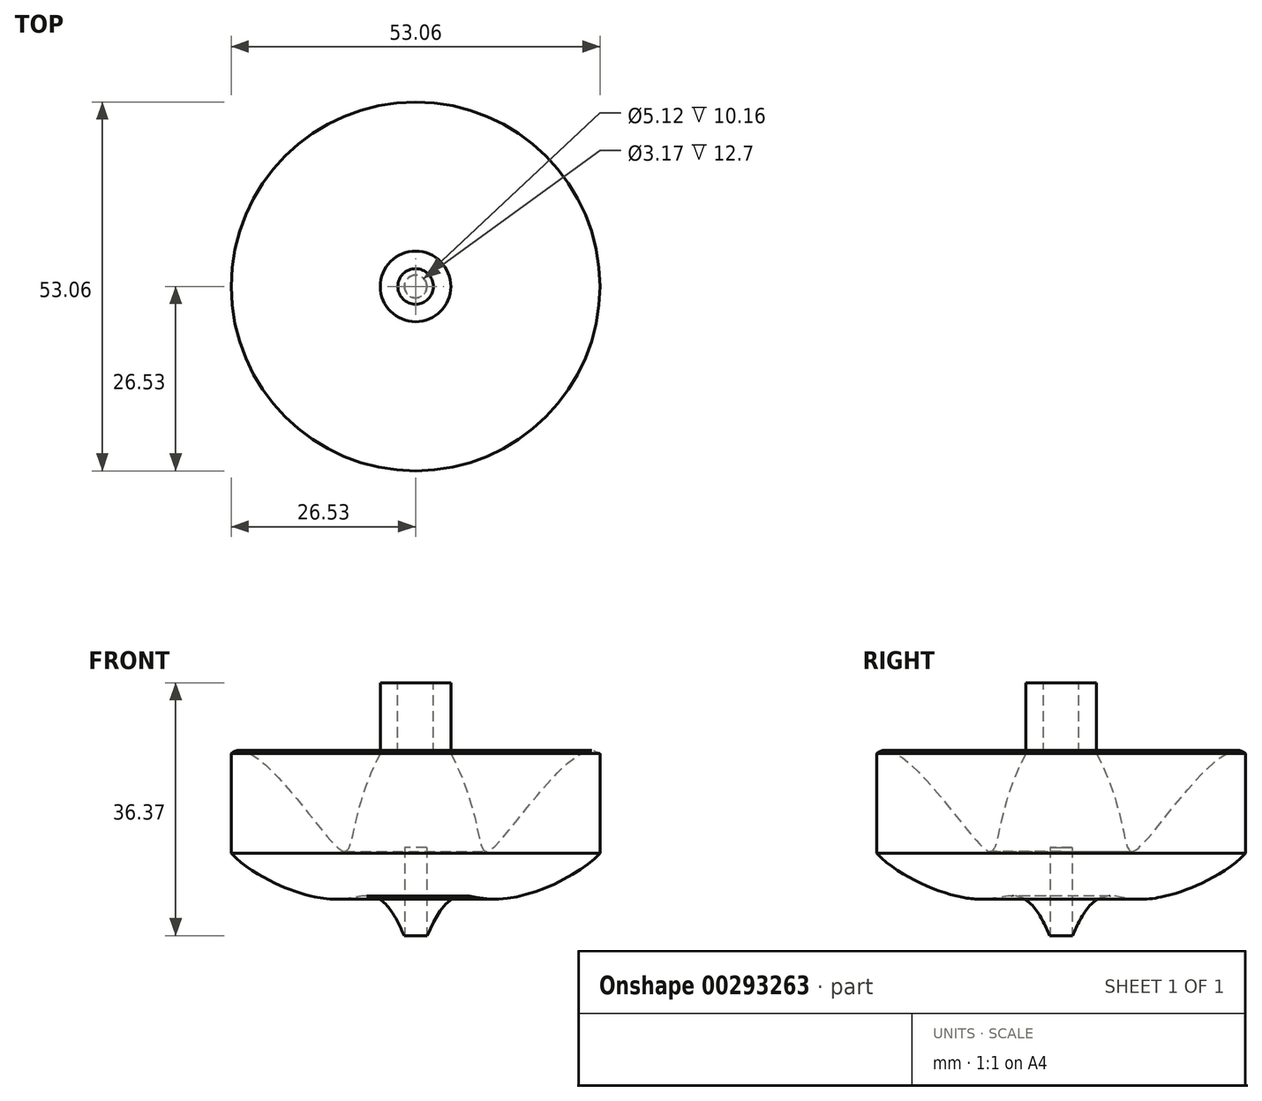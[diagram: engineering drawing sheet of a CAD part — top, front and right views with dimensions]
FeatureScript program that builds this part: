
annotation { "Feature Type Name" : "Feature", "Feature Type Description" : "" }
export const myFeature = defineFeature(function(context is Context, id is Id, definition is map)
    precondition{}
    {
        {
            var Q0;
            Q0=qCreatedBy(makeId("Front.planeOp"),FACE);
            var sketch = newSketch(context, id + "F0", { "sketchPlane" : qUnion([Q0])});
            skLineSegment(sketch, "E0", {"start": v(0, 0) * mm, "end": v(1.65, 0) * mm});
            skPoint(sketch, "E1", {"position": v(11.05, 5.23) * mm});
            skPoint(sketch, "E2", {"position": v(26.53, 11.84) * mm});
            skPoint(sketch, "E3", {"position": v(26.53, 26.2) * mm});
            skPoint(sketch, "E4", {"position": v(11.05, 12.52) * mm});
            skPoint(sketch, "E5", {"position": v(5.08, 26.2) * mm});
            skPoint(sketch, "E6", {"position": v(5.08, 36.37) * mm});
            skPoint(sketch, "E7", {"position": v(0, 36.37) * mm});
            skLineSegment(sketch, "E8", {"start": v(26.53, 11.84) * mm, "end": v(26.53, 26.2) * mm});
            skLineSegment(sketch, "E9", {"start": v(0, 36.37) * mm, "end": v(5.08, 36.37) * mm});
            skLineSegment(sketch, "E10", {"start": v(0, 36.37) * mm, "end": v(0, 0) * mm});
            skLineSegment(sketch, "E11", {"start": v(5.08, 36.37) * mm, "end": v(5.08, 26.2) * mm});
            skFitSpline(sketch, "E12", {"points": [v(5.08, 26.2) * mm, v(11.05, 12.52) * mm, v(26.53, 26.2) * mm], "startDerivative": vector(32.65, -62.24) * mm, "endDerivative": vector(19.41, -17.14) * mm});
            skFitSpline(sketch, "E13", {"points": [v(1.65, 0) * mm, v(11.05, 5.23) * mm, v(26.53, 11.84) * mm], "startDerivative": vector(22.47, 52.96) * mm, "endDerivative": vector(16.44, 18.16) * mm});
            skPoint(sketch, "E14", {"position": v(7.82, 19.55) * mm});
            skPoint(sketch, "E15", {"position": v(21.1, 24.1) * mm});
            skSolve(sketch);
        }
        {
            var Q0;
            Q0 = qSketchRegion(id + "F0", true);
            var Q1;
            Q1=sQuery(id+"F0.wireOp",EDGE,"E10");
            revolve(context, id + "F1", {"entities" : qUnion([Q0]), "axis" : qUnion([Q1]), "revolveType" : RevolveType.FULL});
        }
        {
            var Q0;
            Q0=makeQuery(id+"F1.opRevolve","SWEPT_FACE",FACE,{"disambiguationData":[OSD([sQuery(id+"F0.wireOp",EDGE,"E9")])]});
            var sketch = newSketch(context, id + "F2", { "sketchPlane" : qUnion([Q0])});
            skCircle(sketch, "E16", {"center": v(0, 0) * mm, "radius": 2.56 * mm});
            skSolve(sketch);
        }
        {
            var Q0;
            Q0 = qSketchRegion(id + "F2", true);
            extrude(context, id + "F3", {"entities" : qUnion([Q0]), "operationType" : NewBodyOperationType.REMOVE, "oppositeDirection" : true, "depth" : 10.16 * mm});
        }
        {
            var Q0;
            Q0=qCreatedBy(makeId("Top.planeOp"),FACE);
            var sketch = newSketch(context, id + "F4", { "sketchPlane" : qUnion([Q0])});
            skCircle(sketch, "E17", {"center": v(0, 0) * mm, "radius": 1.59 * mm});
            skSolve(sketch);
        }
        {
            var Q0;
            Q0 = qSketchRegion(id + "F4", true);
            extrude(context, id + "F5", {"entities" : qUnion([Q0]), "operationType" : NewBodyOperationType.REMOVE, "depth" : 12.7 * mm});
        }
    });
